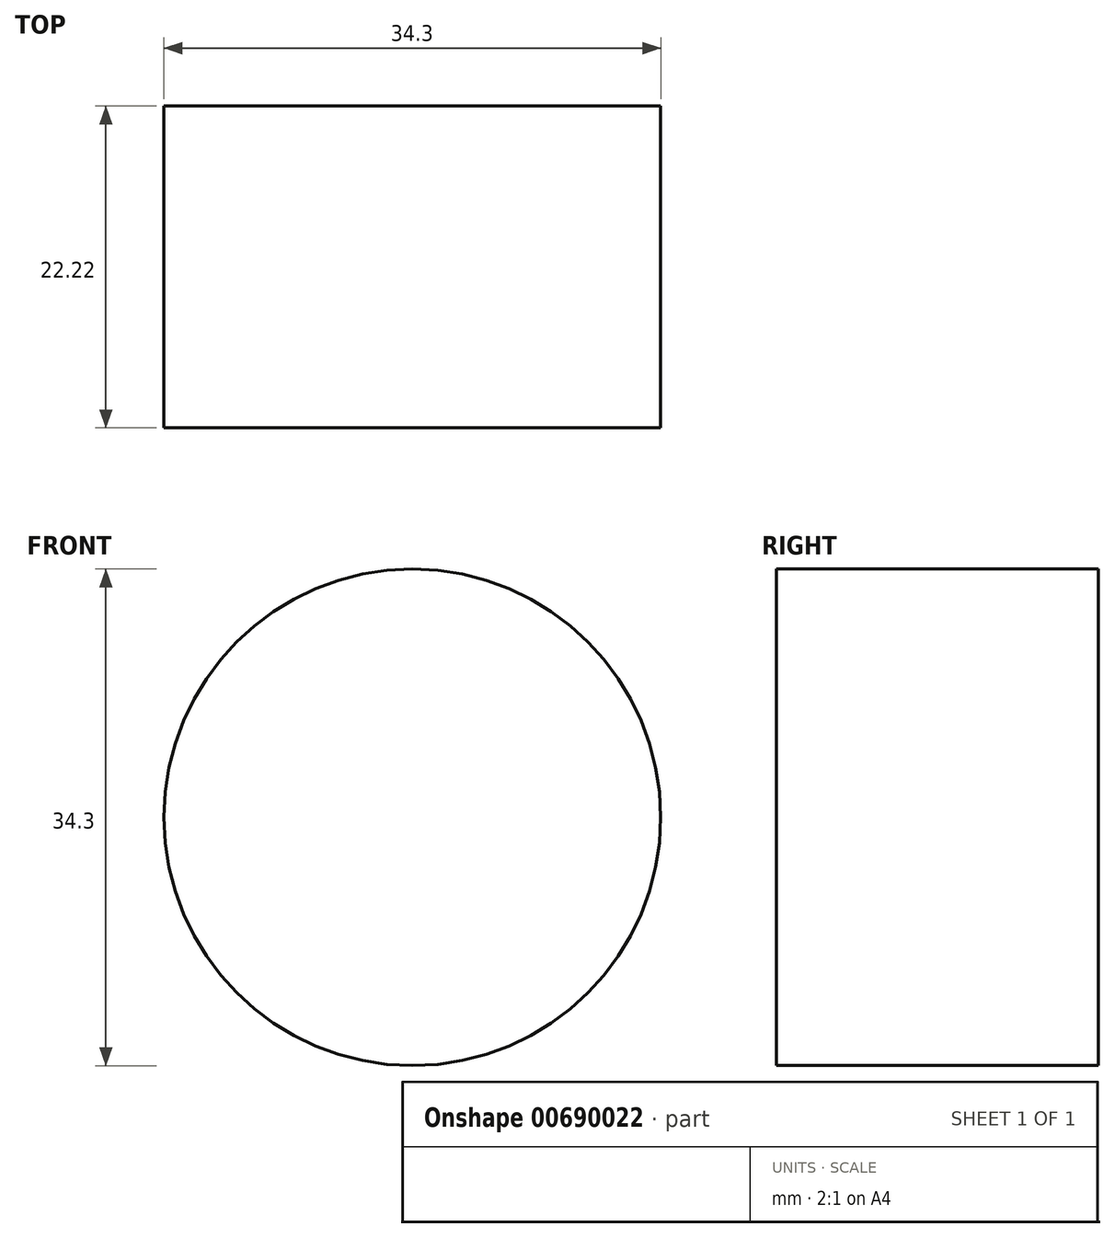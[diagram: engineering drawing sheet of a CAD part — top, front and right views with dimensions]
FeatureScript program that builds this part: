
annotation { "Feature Type Name" : "Feature", "Feature Type Description" : "" }
export const myFeature = defineFeature(function(context is Context, id is Id, definition is map)
    precondition{}
    {
        {
            var Q0;
            Q0=qCreatedBy(makeId("Front.planeOp"),FACE);
            var sketch = newSketch(context, id + "F0", { "sketchPlane" : qUnion([Q0])});
            skCircle(sketch, "E0", {"center": v(0, 0) * mm, "radius": 17.15 * mm});
            skSolve(sketch);
        }
        {
            var Q0;
            Q0 = qSketchRegion(id + "F0", true);
            extrude(context, id + "F1", {"entities" : qUnion([Q0]), "endBound" : BoundingType.SYMMETRIC, "depth" : 22.22 * mm, "offsetDistance" : 25.4 * mm});
        }
    });
